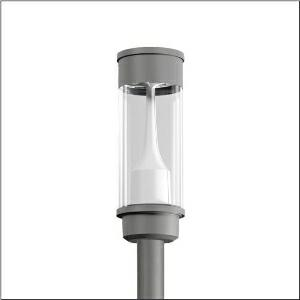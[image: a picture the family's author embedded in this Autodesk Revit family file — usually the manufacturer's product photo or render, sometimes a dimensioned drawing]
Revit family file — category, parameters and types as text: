
# Revit family: litepole_iq___st1_2a_5xa5415ef14h_6754
name_source: partatom
category: Lighting Fixtures
units: mm (PartAtom-declared; Revit-internal decimal feet)

## family parameters
Cut with Voids When Loaded = No
Host = Face
Light Source = No
Part Type = Normal
Room Calculation Point = No
Round Connector Dimension = Use Diameter
Shared = No

## types (1)
- --- (1 x LED, 1540 lm, 10.5 W, 3000K)
    Apparent Load = 11 VA
    CIE Flux Codes = 22 61 93 96 100
    Color Rendering = 70
    Color Temperature = 3000K
    Default Elevation = 1800 mm
    Description = Litepole iQ, mast luminaire, Module 540 iQ-SR, primary light control with 3 zone facetted reflector, of plastic, silver coated, highly specular, structured, primary optical cover: cover, of PMMA, transparent, light distribution: ST1.2a, light emission: direct distribution, primary light characteristic: asymmetric, installation type: post-top, LED, High Power LED, rated luminous flux: 1.540lm, luminous efficacy: 147lm/W, light colour: 730, colour temperature: 3000K, control gear: iQ Street-Remote, control: Auto-Match, Temp-Guard, Lumen-Switch, Night-Set, Smart-Wire, Light-Fading, Desk-Remote (wireless, voltage-free reading and setting of iQ features in the workshop via application-optimized NFC function/RFID function), optimised constant luminous flux control (CLO 2.0), Street-Remote, pre-setting: logarithmic dimming characteristic, with terminal, 6-pole, max. 2.5mm², mains connection: 230..240V, AC, 50/60Hz, start of lifetime: 11W, end of service life: 11W, reduction: 5W, luminaire housing, upper part, of glass-fibre reinforced polyester, coated, Siteco® metallic grey (DB 702S), diameter: 210mm, height: 590mm, spigot size: d x l = 76 x 70mm (post-top) | with reducer (optional accessory) 60 x 70mm, mounting height: 3..5m, post-top mast mounting element, of diecast aluminium, coated, Siteco® metallic grey (DB 702S), Module 540 iQ-SR, traffic white (RAL 9016), equipment: standard, protection rating (complete): IP65, insulation class (complete): insulation class II (safety insulation), certification: CE, ENEC, VDE, packaging unit: 1 piece

Light Distribution: ST1.2a
    Height = 590 mm
    Lamp = 1 x LED
    Lamp Light Flux = 1540 lm
    Lamp Power = 10.5 W
    Lamp count = 1
    Length = 220 mm
    Luminous efficacy = 147 lm/W
    Manufacturer = Siteco
    ModVariant = No
    Model = 5XA5415EF14H
    Number of Poles = 1
    OnlyDefault = Yes
    Power Factor = 1
    Product Name = Litepole iQ | ST1.2a
    Product group = mast luminaire | pylon top
    ProductGroupID = 6100
    Protection Class = Protection class II
    Protection Degree = IP 65
    RLX_Detail_Level = 1
    RLX_Emergency_Light_Flux = 0 lm
    RLX_Emergency_Type = 0
    RLX_Emergency_Type_DB = No
    RlxData = <blob elided: 72001 chars, md5=9764a8b5>
    Socket = socket
    Standby Power = 0 W
    System Light Flux = 1540 lm
    System Power = 11 W
    Type Comments = factory setting: luminous flux: 100 % | dim-lin: 254 | 419 mA
    Type Image = l_1006025.jpg
    URL = http://relux.com
    VarID = @adj_158337
    Voltage = 0 V
    Weight = 0.00 kg
    Width = 0 mm  [stored 0 ft]

note: [stored X ft] marks values corroborated as IEEE doubles in the binary element streams (Revit-internal decimal feet)

## geometry (parser evidence)
native form markers: Blend x4, Sweep x9
no freeform markers — native parametric forms only
